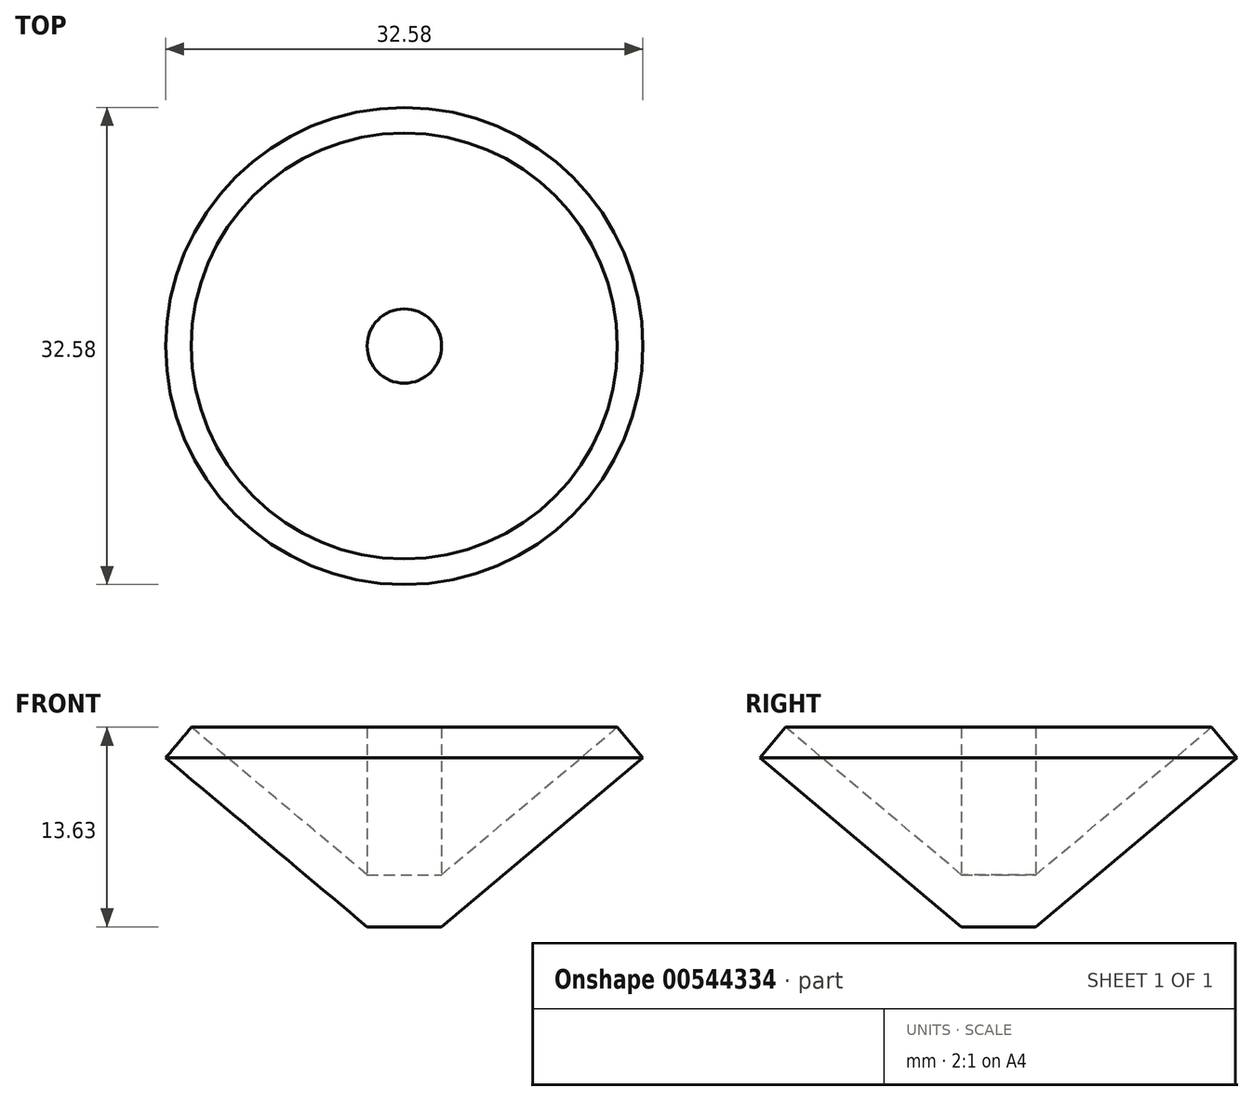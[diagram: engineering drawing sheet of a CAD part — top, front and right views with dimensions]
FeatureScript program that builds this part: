
annotation { "Feature Type Name" : "Feature", "Feature Type Description" : "" }
export const myFeature = defineFeature(function(context is Context, id is Id, definition is map)
    precondition{}
    {
        {
            var Q0;
            Q0=qCreatedBy(makeId("Front.planeOp"),FACE);
            var sketch = newSketch(context, id + "F0", { "sketchPlane" : qUnion([Q0])});
            skLineSegment(sketch, "E0.bottom", {"start": v(0, 0) * mm, "end": v(2.54, 0) * mm});
            skLineSegment(sketch, "E0.left", {"start": v(0, 0) * mm, "end": v(0, 13.63) * mm});
            skLineSegment(sketch, "E0.right", {"start": v(2.54, 3.55) * mm, "end": v(2.54, 13.63) * mm});
            skLineSegment(sketch, "E1", {"start": v(2.54, 0) * mm, "end": v(16.3, 11.54) * mm});
            skLineSegment(sketch, "E2", {"start": v(16.3, 11.54) * mm, "end": v(14.54, 13.63) * mm});
            skLineSegment(sketch, "E3", {"start": v(14.54, 13.63) * mm, "end": v(2.54, 3.55) * mm});
            skLineSegment(sketch, "E4", {"start": v(2.54, 13.63) * mm, "end": v(0, 13.63) * mm});
            skSolve(sketch);
        }
        {
            var Q0;
            Q0=makeQuery(id+"F0.imprint","IMPRINT",FACE,{"disambiguationData":[TD([[makeQuery(id+"F0.imprint","IMPRINT",EDGE,{"derivedFrom":sQuery(id+"F0.wireOp",EDGE,"E0.bottom")}),1.0]])]});
            var Q1;
            Q1=sQuery(id+"F0.wireOp",EDGE,"E0.left");
            revolve(context, id + "F1", {"entities" : qUnion([Q0]), "axis" : qUnion([Q1]), "revolveType" : RevolveType.FULL});
        }
    });
